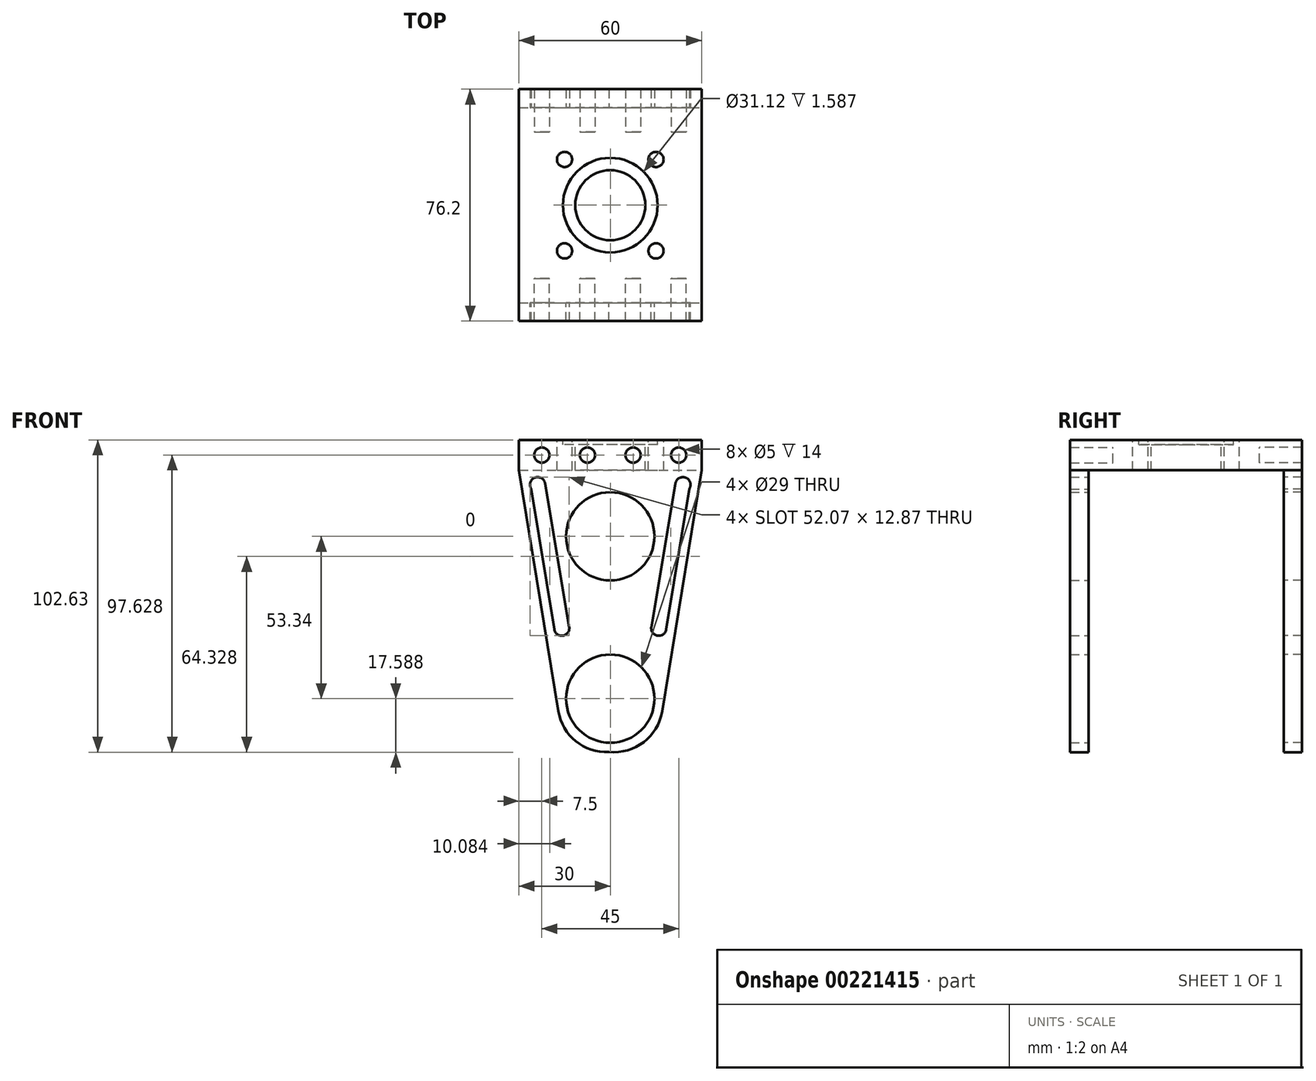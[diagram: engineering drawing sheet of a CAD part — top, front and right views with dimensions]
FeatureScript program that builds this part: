
annotation { "Feature Type Name" : "Feature", "Feature Type Description" : "" }
export const myFeature = defineFeature(function(context is Context, id is Id, definition is map)
    precondition{}
    {
        {
            var Q0;
            Q0=qCreatedBy(makeId("Front.planeOp"),FACE);
            var sketch = newSketch(context, id + "F0", { "sketchPlane" : qUnion([Q0])});
            skPoint(sketch, "E0.middle", {"position": v(0, 0) * mm});
            skLineSegment(sketch, "E1", {"start": v(30, 66.53) * mm, "end": v(-30, 66.53) * mm});
            skLineSegment(sketch, "E2", {"start": v(-30, 56.53) * mm, "end": v(-17.06, -22.61) * mm});
            skLineSegment(sketch, "E3", {"start": v(17.05, -22.68) * mm, "end": v(30, 56.53) * mm});
            skCircle(sketch, "E4", {"center": v(0, 34.83) * mm, "radius": 14.5 * mm});
            skLineSegment(sketch, "E5", {"start": v(0, 66.53) * mm, "end": v(0, 34.83) * mm, "construction": true});
            skCircle(sketch, "E6", {"center": v(0, -18.51) * mm, "radius": 14.5 * mm});
            skLineSegment(sketch, "E7", {"start": v(-18.41, 4.24) * mm, "end": v(-25.96, 50.39) * mm});
            skLineSegment(sketch, "E8", {"start": v(-21.4, 52.19) * mm, "end": v(-13.48, 5.07) * mm});
            skPoint(sketch, "E9.visualSharp", {"position": v(-21.8, 54.53) * mm});
            skPoint(sketch, "E10.visualSharp", {"position": v(-26.26, 52.27) * mm});
            skPoint(sketch, "E11.visualSharp", {"position": v(-18.2, 2.92) * mm});
            skLineSegment(sketch, "E11.filletArc", {"start": v(-18.41, 4.24) * mm, "end": v(-18.41, 4.24) * mm});
            skPoint(sketch, "E12.visualSharp", {"position": v(-8.18, -26.45) * mm});
            skPoint(sketch, "E13.visualSharp", {"position": v(-12.87, -48.24) * mm});
            skArc(sketch, "E13.filletArc", {"start": v(-17.06, -22.61) * mm, "mid": v(-11.3, -32.5) * mm, "end": v(-0.43, -36) * mm});
            skPoint(sketch, "E14.visualSharp", {"position": v(12.87, -48.24) * mm});
            skArc(sketch, "E14.filletArc", {"start": v(-0.43, -36) * mm, "mid": v(10.96, -32.82) * mm, "end": v(17.05, -22.68) * mm});
            skLineSegment(sketch, "E15", {"start": v(-30, 56.53) * mm, "end": v(30, 56.53) * mm});
            skLineSegment(sketch, "E16", {"start": v(-30, 66.53) * mm, "end": v(-30, 56.53) * mm});
            skLineSegment(sketch, "E17", {"start": v(30, 56.53) * mm, "end": v(30, 66.53) * mm});
            skCircle(sketch, "E18", {"center": v(-22.5, 61.53) * mm, "radius": 2.5 * mm});
            skCircle(sketch, "E19.1.0.0", {"center": v(-7.5, 61.53) * mm, "radius": 2.5 * mm});
            skCircle(sketch, "E19.2.0.0", {"center": v(7.5, 61.53) * mm, "radius": 2.5 * mm});
            skCircle(sketch, "E19.3.0.0", {"center": v(22.5, 61.53) * mm, "radius": 2.5 * mm});
            skLineSegment(sketch, "E19.direction1", {"start": v(-22.5, 61.53) * mm, "end": v(-7.5, 61.53) * mm, "construction": true});
            skArc(sketch, "E20", {"start": v(-18.41, 4.24) * mm, "mid": v(-15.53, 2.2) * mm, "end": v(-13.48, 5.07) * mm});
            skArc(sketch, "E21", {"start": v(-21.4, 52.19) * mm, "mid": v(-24.8, 54.1) * mm, "end": v(-25.96, 50.39) * mm});
            skLineSegment(sketch, "E22.MirrorCS", {"start": v(21.4, 52.19) * mm, "end": v(13.48, 5.07) * mm});
            skLineSegment(sketch, "E23.MirrorCS", {"start": v(18.41, 4.24) * mm, "end": v(25.96, 50.39) * mm});
            skArc(sketch, "E24.MirrorCS", {"start": v(21.4, 52.19) * mm, "mid": v(24.8, 54.1) * mm, "end": v(25.96, 50.39) * mm});
            skArc(sketch, "E25.MirrorCS", {"start": v(18.41, 4.24) * mm, "mid": v(15.53, 2.2) * mm, "end": v(13.48, 5.07) * mm});
            skSolve(sketch);
        }
        {
            var Q0;
            Q0=qSketchRegion(id+"F0",true);
            extrude(context, id + "F1", {"entities" : qUnion([Q0]), "depth" : 6 * mm});
        }
        {
            var Q0;
            Q0=makeQuery(id+"F0.imprint","IMPRINT",FACE,{"disambiguationData":[TD([[makeQuery(id+"F0.imprint","IMPRINT",EDGE,{"derivedFrom":sQuery(id+"F0.wireOp",EDGE,"E1")}),1.0]])]});
            var Q1;
            Q1=makeQuery(id+"F0.imprint","IMPRINT",FACE,{"disambiguationData":[TD([[makeQuery(id+"F0.imprint","IMPRINT",EDGE,{"derivedFrom":sQuery(id+"F0.wireOp",EDGE,"E18")}),1.0]])]});
            var Q2;
            Q2=makeQuery(id+"F0.imprint","IMPRINT",FACE,{"disambiguationData":[TD([[makeQuery(id+"F0.imprint","IMPRINT",EDGE,{"derivedFrom":sQuery(id+"F0.wireOp",EDGE,"E19.1.0.0")}),1.0]])]});
            var Q3;
            Q3=makeQuery(id+"F0.imprint","IMPRINT",FACE,{"disambiguationData":[TD([[makeQuery(id+"F0.imprint","IMPRINT",EDGE,{"derivedFrom":sQuery(id+"F0.wireOp",EDGE,"E19.2.0.0")}),1.0]])]});
            var Q4;
            Q4=makeQuery(id+"F0.imprint","IMPRINT",FACE,{"disambiguationData":[TD([[makeQuery(id+"F0.imprint","IMPRINT",EDGE,{"derivedFrom":sQuery(id+"F0.wireOp",EDGE,"E19.3.0.0")}),1.0]])]});
            extrude(context, id + "F2", {"entities" : qUnion([Q0, Q1, Q2, Q3, Q4]), "oppositeDirection" : true, "offsetDistance" : 25 * mm, "depth" : 32.1 * mm});
        }
        {
            var Q0;
            Q0=makeQuery(id+"F0.imprint","IMPRINT",FACE,{"disambiguationData":[TD([[makeQuery(id+"F0.imprint","IMPRINT",EDGE,{"derivedFrom":sQuery(id+"F0.wireOp",EDGE,"E18")}),1.0]])]});
            var Q1;
            Q1=makeQuery(id+"F0.imprint","IMPRINT",FACE,{"disambiguationData":[TD([[makeQuery(id+"F0.imprint","IMPRINT",EDGE,{"derivedFrom":sQuery(id+"F0.wireOp",EDGE,"E19.1.0.0")}),1.0]])]});
            var Q2;
            Q2=makeQuery(id+"F0.imprint","IMPRINT",FACE,{"disambiguationData":[TD([[makeQuery(id+"F0.imprint","IMPRINT",EDGE,{"derivedFrom":sQuery(id+"F0.wireOp",EDGE,"E19.2.0.0")}),1.0]])]});
            var Q3;
            Q3=makeQuery(id+"F0.imprint","IMPRINT",FACE,{"disambiguationData":[TD([[makeQuery(id+"F0.imprint","IMPRINT",EDGE,{"derivedFrom":sQuery(id+"F0.wireOp",EDGE,"E19.3.0.0")}),1.0]])]});
            extrude(context, id + "F3", {"entities" : qUnion([Q0, Q1, Q2, Q3]), "operationType" : NewBodyOperationType.REMOVE, "oppositeDirection" : true, "depth" : 8 * mm});
        }
        {
            var Q0;
            Q0=makeQuery(id+"F1.opExtrude","SWEPT_BODY",BODY,{"disambiguationData":[OSD([sQuery(id+"F0.wireOp",EDGE,"E1"),sQuery(id+"F0.wireOp",EDGE,"E2"),sQuery(id+"F0.wireOp",EDGE,"SYUOTkIr-tYDY-Dmn5-QcU2-4CVYqx2D2yp1"),sQuery(id+"F0.wireOp",EDGE,"E3"),sQuery(id+"F0.wireOp",EDGE,"E4"),sQuery(id+"F0.wireOp",EDGE,"E6"),sQuery(id+"F0.wireOp",EDGE,"E7"),sQuery(id+"F0.wireOp",EDGE,"OxaRfaqW-ItMm-Otgn-Riyy-IPCwFij4wlHa"),sQuery(id+"F0.wireOp",EDGE,"E8"),sQuery(id+"F0.wireOp",EDGE,"RyqfKOtT-yPM8-Sfqq-ylPv-WJ9zvdXIONvg"),sQuery(id+"F0.wireOp",EDGE,"UMvfX0qj-cdd0-jv7Y-gCsA-kVYkeAgtTEpR"),sQuery(id+"F0.wireOp",EDGE,"eBsDUVpw-Hlep-jQpn-DiYE-6YDLSgGNxe9n"),sQuery(id+"F0.wireOp",EDGE,"r3Qx0Ujx-bb2U-5Zuz-YPRV-eggkf8KlDdbs"),sQuery(id+"F0.wireOp",EDGE,"igt9e6wt-k0kr-WNeF-lPce-3P5oyZGuuQ9H"),sQuery(id+"F0.wireOp",EDGE,"E9.filletArc"),sQuery(id+"F0.wireOp",EDGE,"E10.filletArc"),sQuery(id+"F0.wireOp",EDGE,"E11.filletArc"),sQuery(id+"F0.wireOp",EDGE,"E12.filletArc"),sQuery(id+"F0.wireOp",EDGE,"59ca9dbd-221c-4f41-a9c7-bfba9f8e5bf8.filletArc"),sQuery(id+"F0.wireOp",EDGE,"7ced0f47-db27-4fa9-bf7f-120a9fff237b.filletArc"),sQuery(id+"F0.wireOp",EDGE,"8cfca6ee-5c72-4fe0-a6e4-4b02504b93ad.filletArc"),sQuery(id+"F0.wireOp",EDGE,"6a8a8492-c00a-448f-a719-a00f6dea5276.filletArc"),sQuery(id+"F0.wireOp",EDGE,"E13.filletArc"),sQuery(id+"F0.wireOp",EDGE,"E14.filletArc"),sQuery(id+"F0.wireOp",EDGE,"E16"),sQuery(id+"F0.wireOp",EDGE,"E17"),sQuery(id+"F0.wireOp",EDGE,"E18"),sQuery(id+"F0.wireOp",EDGE,"E19.1.0.0"),sQuery(id+"F0.wireOp",EDGE,"E19.2.0.0"),sQuery(id+"F0.wireOp",EDGE,"E19.3.0.0")])]});
            var Q1;
            Q1=makeQuery(id+"F2.opExtrude","CAP_FACE",FACE,{"disambiguationData":[OSD([sQuery(id+"F0.wireOp",EDGE,"E1"),sQuery(id+"F0.wireOp",EDGE,"E15"),sQuery(id+"F0.wireOp",EDGE,"E16"),sQuery(id+"F0.wireOp",EDGE,"E17")])],"isStart":false});
            mirror(context, id + "F4", {"entities" : qUnion([Q0]), "mirrorPlane" : qUnion([Q1])});
        }
        {
            var Q0;
            Q0=makeQuery(id+"F2.opExtrude","SWEPT_BODY",BODY,{"disambiguationData":[OSD([sQuery(id+"F0.wireOp",EDGE,"E1"),sQuery(id+"F0.wireOp",EDGE,"E15"),sQuery(id+"F0.wireOp",EDGE,"E16"),sQuery(id+"F0.wireOp",EDGE,"E17")])]});
            var Q1;
            Q1=makeQuery(id+"F2.opExtrude","CAP_FACE",FACE,{"disambiguationData":[OSD([sQuery(id+"F0.wireOp",EDGE,"E1"),sQuery(id+"F0.wireOp",EDGE,"E15"),sQuery(id+"F0.wireOp",EDGE,"E16"),sQuery(id+"F0.wireOp",EDGE,"E17")])],"isStart":false});
            mirror(context, id + "F5", {"operationType" : NewBodyOperationType.ADD, "entities" : qUnion([Q0]), "mirrorPlane" : qUnion([Q1])});
        }
        {
            var Q0;
            {var subQ0=makeQuery(id+"F2.opExtrude","SWEPT_FACE",FACE,{"disambiguationData":[OSD([sQuery(id+"F0.wireOp",EDGE,"E1")])]});Q0=makeQuery(id+"F5.boolean.opBoolean","MERGE",FACE,{"derivedFrom":[subQ0,makeQuery(id+"F5.opPattern","COPY",FACE,{"derivedFrom":subQ0,"instanceName":"1"})]});}
            var sketch = newSketch(context, id + "F6", { "sketchPlane" : qUnion([Q0])});
            skCircle(sketch, "E26", {"center": v(0, 32.1) * mm, "radius": 11.5 * mm});
            skLineSegment(sketch, "E27", {"start": v(0, 32.1) * mm, "end": v(0, 0) * mm, "construction": true});
            skPoint(sketch, "E28", {"position": v(-30, 32.1) * mm});
            skSolve(sketch);
        }
        {
            var Q0;
            Q0 = qSketchRegion(id + "F6", true);
            extrude(context, id + "F7", {"entities" : qUnion([Q0]), "operationType" : NewBodyOperationType.REMOVE, "endBound" : BoundingType.UP_TO_NEXT, "oppositeDirection" : true, "depth" : 25 * mm});
        }
        {
            var Q0;
            {var subQ0=makeQuery(id+"F2.opExtrude","SWEPT_FACE",FACE,{"disambiguationData":[OSD([sQuery(id+"F0.wireOp",EDGE,"E1")])]});Q0=makeQuery(id+"F5.boolean.opBoolean","MERGE",FACE,{"derivedFrom":[subQ0,makeQuery(id+"F5.opPattern","COPY",FACE,{"derivedFrom":subQ0,"instanceName":"1"})]});}
            var sketch = newSketch(context, id + "F8", { "sketchPlane" : qUnion([Q0])});
            skLineSegment(sketch, "E29.bottom", {"start": v(-15.03, 47.13) * mm, "end": v(15.03, 47.13) * mm, "construction": true});
            skLineSegment(sketch, "E29.top", {"start": v(-15.03, 17.07) * mm, "end": v(15.03, 17.07) * mm, "construction": true});
            skLineSegment(sketch, "E29.left", {"start": v(-15.03, 47.13) * mm, "end": v(-15.03, 17.07) * mm, "construction": true});
            skLineSegment(sketch, "E29.right", {"start": v(15.03, 47.13) * mm, "end": v(15.03, 17.07) * mm, "construction": true});
            skPoint(sketch, "E29.middle", {"position": v(0, 32.1) * mm});
            skCircle(sketch, "E30", {"center": v(-15.03, 47.13) * mm, "radius": 2.5 * mm});
            skCircle(sketch, "E31", {"center": v(-15.03, 17.07) * mm, "radius": 2.5 * mm});
            skCircle(sketch, "E32", {"center": v(15.03, 47.13) * mm, "radius": 2.5 * mm});
            skCircle(sketch, "E33", {"center": v(15.03, 17.07) * mm, "radius": 2.5 * mm});
            skSolve(sketch);
        }
        {
            var Q0;
            Q0 = qSketchRegion(id + "F8", true);
            var Q1;
            {var subQ0=makeQuery(id+"F2.opExtrude","SWEPT_FACE",FACE,{"disambiguationData":[OSD([sQuery(id+"F0.wireOp",EDGE,"E15")])]});Q1=makeQuery(id+"F5.boolean.opBoolean","MERGE",FACE,{"derivedFrom":[subQ0,makeQuery(id+"F5.opPattern","COPY",FACE,{"derivedFrom":subQ0,"instanceName":"1"})]});}
            extrude(context, id + "F9", {"entities" : qUnion([Q0]), "operationType" : NewBodyOperationType.REMOVE, "endBound" : BoundingType.UP_TO_SURFACE, "oppositeDirection" : true, "endBoundEntityFace" : qUnion([Q1]), "depth" : 25 * mm});
        }
        {
            var Q0;
            {var subQ0=makeQuery(id+"F2.opExtrude","SWEPT_FACE",FACE,{"disambiguationData":[OSD([sQuery(id+"F0.wireOp",EDGE,"E1")])]});Q0=makeQuery(id+"F5.boolean.opBoolean","MERGE",FACE,{"derivedFrom":[subQ0,makeQuery(id+"F5.opPattern","COPY",FACE,{"derivedFrom":subQ0,"instanceName":"1"})]});}
            var sketch = newSketch(context, id + "F10", { "sketchPlane" : qUnion([Q0])});
            skCircle(sketch, "E34", {"center": v(0, 32.1) * mm, "radius": 15.56 * mm});
            skSolve(sketch);
        }
        {
            var Q0;
            Q0 = qSketchRegion(id + "F10", true);
            extrude(context, id + "F11", {"entities" : qUnion([Q0]), "operationType" : NewBodyOperationType.REMOVE, "oppositeDirection" : true, "depth" : 1.59 * mm});
        }
    });
